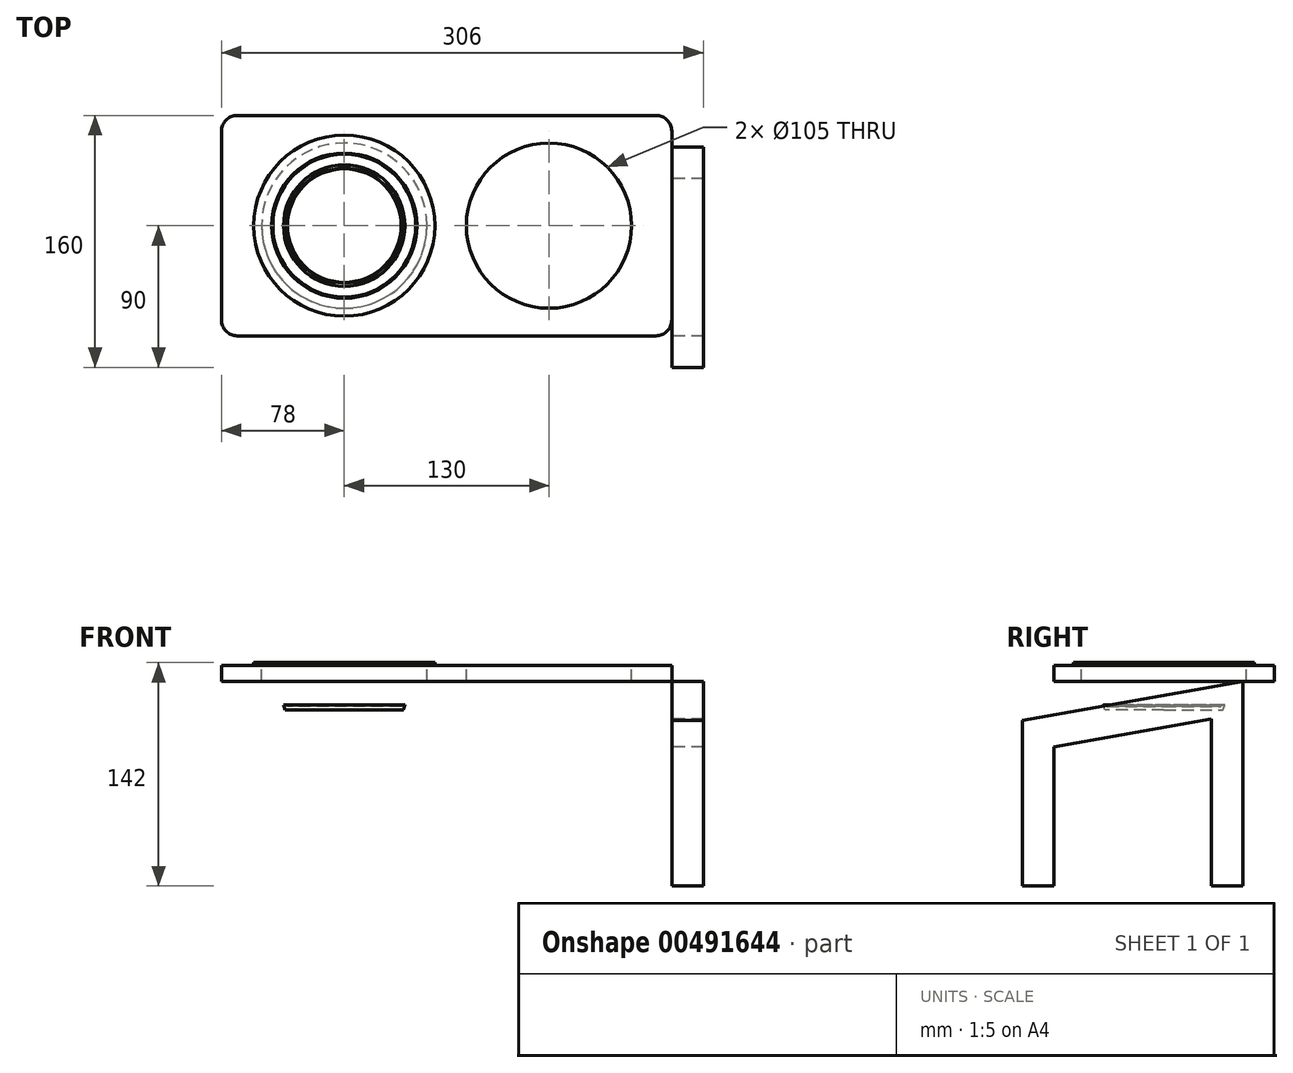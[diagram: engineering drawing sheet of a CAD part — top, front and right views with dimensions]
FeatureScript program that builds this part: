
annotation { "Feature Type Name" : "Feature", "Feature Type Description" : "" }
export const myFeature = defineFeature(function(context is Context, id is Id, definition is map)
    precondition{}
    {
        {
            var Q0;
            Q0=qCreatedBy(makeId("Top.planeOp"),FACE);
            var sketch = newSketch(context, id + "F0", { "sketchPlane" : qUnion([Q0])});
            skCircle(sketch, "E0", {"center": v(0, 0) * mm, "radius": 57.5 * mm});
            skSolve(sketch);
        }
        {
            var Q0;
            Q0 = qSketchRegion(id + "F0", true);
            extrude(context, id + "F1", {"entities" : qUnion([Q0]), "oppositeDirection" : true, "depth" : 30 * mm});
        }
        {
            var Q0;
            Q0=qCreatedBy(makeId("Front.planeOp"),FACE);
            var sketch = newSketch(context, id + "F2", { "sketchPlane" : qUnion([Q0])});
            skLineSegment(sketch, "E1", {"start": v(57.5, -2) * mm, "end": v(47.5, -2) * mm});
            skLineSegment(sketch, "E2", {"start": v(47.5, -2) * mm, "end": v(37.5, -30) * mm});
            skLineSegment(sketch, "E3", {"start": v(37.5, -30) * mm, "end": v(57.5, -30) * mm});
            skLineSegment(sketch, "E4", {"start": v(57.5, -30) * mm, "end": v(57.5, -2) * mm});
            skLineSegment(sketch, "E5", {"start": v(0, -45.75) * mm, "end": v(0, 0) * mm});
            skSolve(sketch);
        }
        {
            var Q0;
            Q0 = qSketchRegion(id + "F2", true);
            var Q1;
            Q1=sQuery(id+"F2.wireOp",EDGE,"E5");
            revolve(context, id + "F3", {"operationType" : NewBodyOperationType.REMOVE, "entities" : qUnion([Q0]), "axis" : qUnion([Q1]), "revolveType" : RevolveType.FULL});
        }
        {
            var Q0;
            Q0=makeQuery(id+"F1.opExtrude","CAP_FACE",FACE,{"disambiguationData":[OSD([sQuery(id+"F0.wireOp",EDGE,"E0")])],"isStart":true});
            shell(context, id + "F4", {"entities" : qUnion([Q0]), "thickness" : 2 * mm});
        }
        {
            var Q0;
            Q0=makeQuery(id+"F3.boolean.opBoolean","COPY",FACE,{"derivedFrom":makeQuery(id+"F3.opRevolve","SWEPT_FACE",FACE,{"disambiguationData":[OSD([sQuery(id+"F2.wireOp",EDGE,"E1")])]})});
            var sketch = newSketch(context, id + "F5", { "sketchPlane" : qUnion([Q0])});
            skLineSegment(sketch, "E6.bottom", {"start": v(-68, 70) * mm, "end": v(198, 70) * mm});
            skLineSegment(sketch, "E6.top", {"start": v(-68, -70) * mm, "end": v(198, -70) * mm});
            skLineSegment(sketch, "E6.left", {"start": v(-78, 60) * mm, "end": v(-78, -60) * mm});
            skLineSegment(sketch, "E6.right", {"start": v(208, 60) * mm, "end": v(208, -60) * mm});
            skCircle(sketch, "E7.0", {"center": v(0, 0) * mm, "radius": 57.5 * mm, "construction": true});
            skCircle(sketch, "E8.1.0.0", {"center": v(130, 0) * mm, "radius": 57.5 * mm, "construction": true});
            skLineSegment(sketch, "E8.direction1", {"start": v(0, 0) * mm, "end": v(130, 0) * mm, "construction": true});
            skPoint(sketch, "E9.visualSharp", {"position": v(-78, 70) * mm});
            skArc(sketch, "E9.filletArc", {"start": v(-68, 70) * mm, "mid": v(-75.07, 67.07) * mm, "end": v(-78, 60) * mm});
            skPoint(sketch, "E10.visualSharp", {"position": v(208, 70) * mm});
            skArc(sketch, "E10.filletArc", {"start": v(208, 60) * mm, "mid": v(205.07, 67.07) * mm, "end": v(198, 70) * mm});
            skPoint(sketch, "E11.visualSharp", {"position": v(208, -70) * mm});
            skArc(sketch, "E11.filletArc", {"start": v(198, -70) * mm, "mid": v(205.07, -67.07) * mm, "end": v(208, -60) * mm});
            skPoint(sketch, "E12.visualSharp", {"position": v(-78, -70) * mm});
            skArc(sketch, "E12.filletArc", {"start": v(-78, -60) * mm, "mid": v(-75.07, -67.07) * mm, "end": v(-68, -70) * mm});
            skSolve(sketch);
        }
        {
            var Q0;
            Q0 = qSketchRegion(id + "F5", true);
            extrude(context, id + "F6", {"entities" : qUnion([Q0]), "depth" : 10 * mm});
        }
        {
            var Q0;
            Q0=makeQuery(id+"F6.opExtrude","SWEPT_FACE",FACE,{"disambiguationData":[OSD([sQuery(id+"F5.wireOp",EDGE,"E6.right")])]});
            var sketch = newSketch(context, id + "F7", { "sketchPlane" : qUnion([Q0])});
            skLineSegment(sketch, "E13", {"start": v(-90, -36.69) * mm, "end": v(50, -12) * mm});
            skLineSegment(sketch, "E14", {"start": v(50, -12) * mm, "end": v(50, -142) * mm});
            skLineSegment(sketch, "E15", {"start": v(50, -142) * mm, "end": v(-90, -142) * mm});
            skLineSegment(sketch, "E16", {"start": v(-90, -142) * mm, "end": v(-90, -36.69) * mm});
            skSolve(sketch);
        }
        {
            var Q0;
            Q0 = qSketchRegion(id + "F7", true);
            extrude(context, id + "F8", {"entities" : qUnion([Q0]), "depth" : 20 * mm});
        }
        {
            var Q0;
            Q0=makeQuery(id+"F8.opExtrude","CAP_FACE",FACE,{"disambiguationData":[OSD([sQuery(id+"F7.wireOp",EDGE,"E13"),sQuery(id+"F7.wireOp",EDGE,"E14"),sQuery(id+"F7.wireOp",EDGE,"E15"),sQuery(id+"F7.wireOp",EDGE,"E16")])],"isStart":false});
            var Q1;
            Q1=makeQuery(id+"F8.opExtrude","SWEPT_FACE",FACE,{"disambiguationData":[OSD([sQuery(id+"F7.wireOp",EDGE,"E15")])]});
            var Q2;
            Q2=makeQuery(id+"F8.opExtrude","CAP_FACE",FACE,{"disambiguationData":[OSD([sQuery(id+"F7.wireOp",EDGE,"E13"),sQuery(id+"F7.wireOp",EDGE,"E14"),sQuery(id+"F7.wireOp",EDGE,"E15"),sQuery(id+"F7.wireOp",EDGE,"E16")])],"isStart":true});
            shell(context, id + "F9", {"entities" : qUnion([Q0, Q1, Q2]), "thickness" : 20 * mm});
        }
        {
            var Q0;
            Q0=makeQuery(id+"F6.opExtrude","CAP_FACE",FACE,{"disambiguationData":[OSD([sQuery(id+"F5.wireOp",EDGE,"E6.bottom"),sQuery(id+"F5.wireOp",EDGE,"E6.top"),sQuery(id+"F5.wireOp",EDGE,"E6.left"),sQuery(id+"F5.wireOp",EDGE,"E6.right"),sQuery(id+"F5.wireOp",EDGE,"E9.filletArc"),sQuery(id+"F5.wireOp",EDGE,"E10.filletArc"),sQuery(id+"F5.wireOp",EDGE,"E11.filletArc"),sQuery(id+"F5.wireOp",EDGE,"E12.filletArc")])],"isStart":true});
            var sketch = newSketch(context, id + "F10", { "sketchPlane" : qUnion([Q0])});
            skCircle(sketch, "E17", {"center": v(0, 0) * mm, "radius": 52.5 * mm});
            skLineSegment(sketch, "E18", {"start": v(65, 70) * mm, "end": v(65, -106.95) * mm, "construction": true});
            skPoint(sketch, "E18.endSnap0", {"position": v(65, -70) * mm});
            skCircle(sketch, "E19.MirrorC", {"center": v(130, 0) * mm, "radius": 52.5 * mm});
            skSolve(sketch);
        }
        {
            var Q0;
            Q0 = qSketchRegion(id + "F10", true);
            extrude(context, id + "F11", {"entities" : qUnion([Q0]), "operationType" : NewBodyOperationType.REMOVE, "oppositeDirection" : true, "depth" : 25 * mm});
        }
    });
